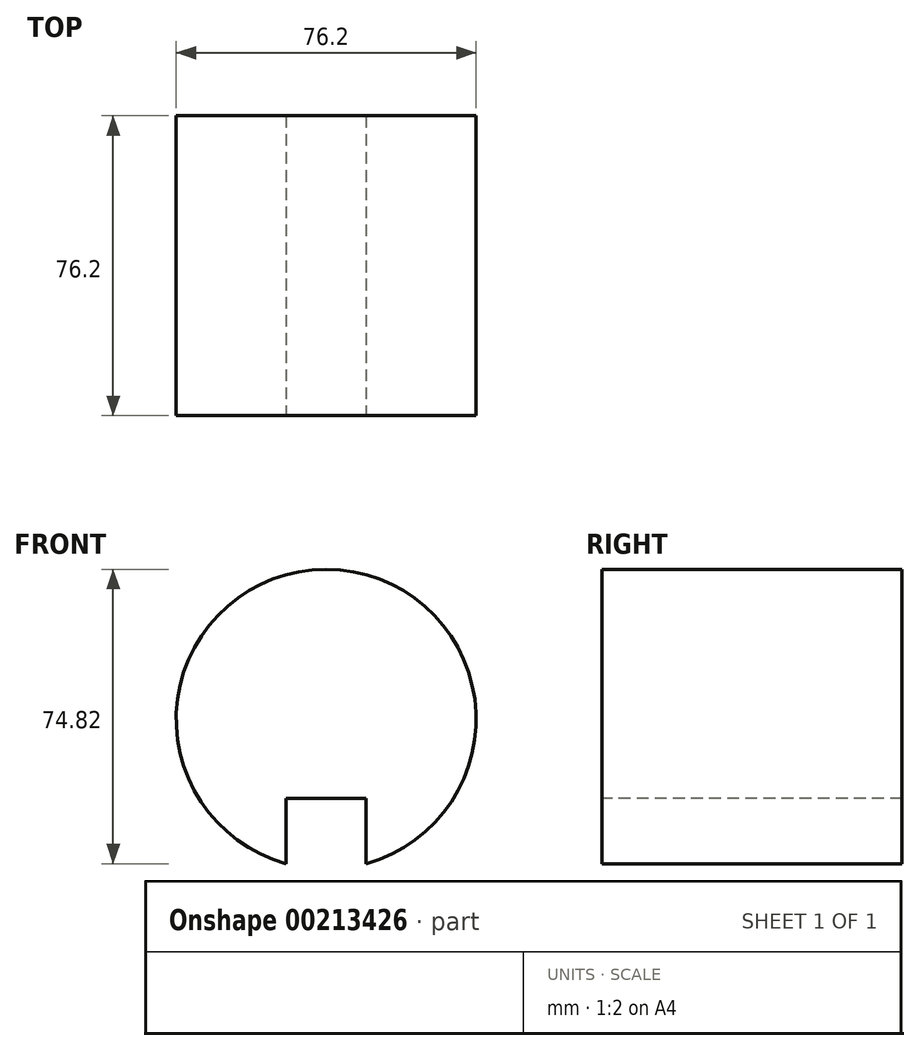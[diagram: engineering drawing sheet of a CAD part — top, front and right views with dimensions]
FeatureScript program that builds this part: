
annotation { "Feature Type Name" : "Feature", "Feature Type Description" : "" }
export const myFeature = defineFeature(function(context is Context, id is Id, definition is map)
    precondition{}
    {
        {
            var Q0;
            Q0=qCreatedBy(makeId("Front.planeOp"),FACE);
            var sketch = newSketch(context, id + "F0", { "sketchPlane" : qUnion([Q0])});
            skCircle(sketch, "E0", {"center": v(0, 0) * mm, "radius": 38.1 * mm});
            skSolve(sketch);
        }
        {
            var Q0;
            Q0=makeQuery(id+"F0.imprint","IMPRINT",FACE,{"disambiguationData":[TD([[makeQuery(id+"F0.imprint","IMPRINT",EDGE,{"derivedFrom":sQuery(id+"F0.wireOp",EDGE,"E0")}),1.0]])]});
            extrude(context, id + "F1", {"entities" : qUnion([Q0]), "depth" : 76.2 * mm});
        }
        {
            var Q0;
            Q0=makeQuery(id+"F1.opExtrude","CAP_FACE",FACE,{"disambiguationData":[OSD([sQuery(id+"F0.wireOp",EDGE,"E0")])],"isStart":false});
            var sketch = newSketch(context, id + "F2", { "sketchPlane" : qUnion([Q0])});
            skLineSegment(sketch, "E1", {"start": v(-10.16, -36.72) * mm, "end": v(-10.16, -20.14) * mm});
            skLineSegment(sketch, "E2", {"start": v(-10.16, -20.14) * mm, "end": v(10.16, -20.14) * mm});
            skLineSegment(sketch, "E3", {"start": v(10.16, -20.14) * mm, "end": v(10.16, -36.72) * mm});
            skSolve(sketch);
        }
        {
            var Q0;
            {var subQ0=sQuery(id+"F2.wireOp",EDGE,"E1");Q0=makeQuery(id+"F2.imprint","IMPRINT",FACE,{"disambiguationData":[TD([[makeQuery(id+"F2.imprint","IMPRINT",EDGE,{"derivedFrom":subQ0}),-1.0]])]});}
            extrude(context, id + "F3", {"entities" : qUnion([Q0]), "operationType" : NewBodyOperationType.REMOVE, "endBound" : BoundingType.THROUGH_ALL, "oppositeDirection" : true, "depth" : 25.4 * mm});
        }
    });
